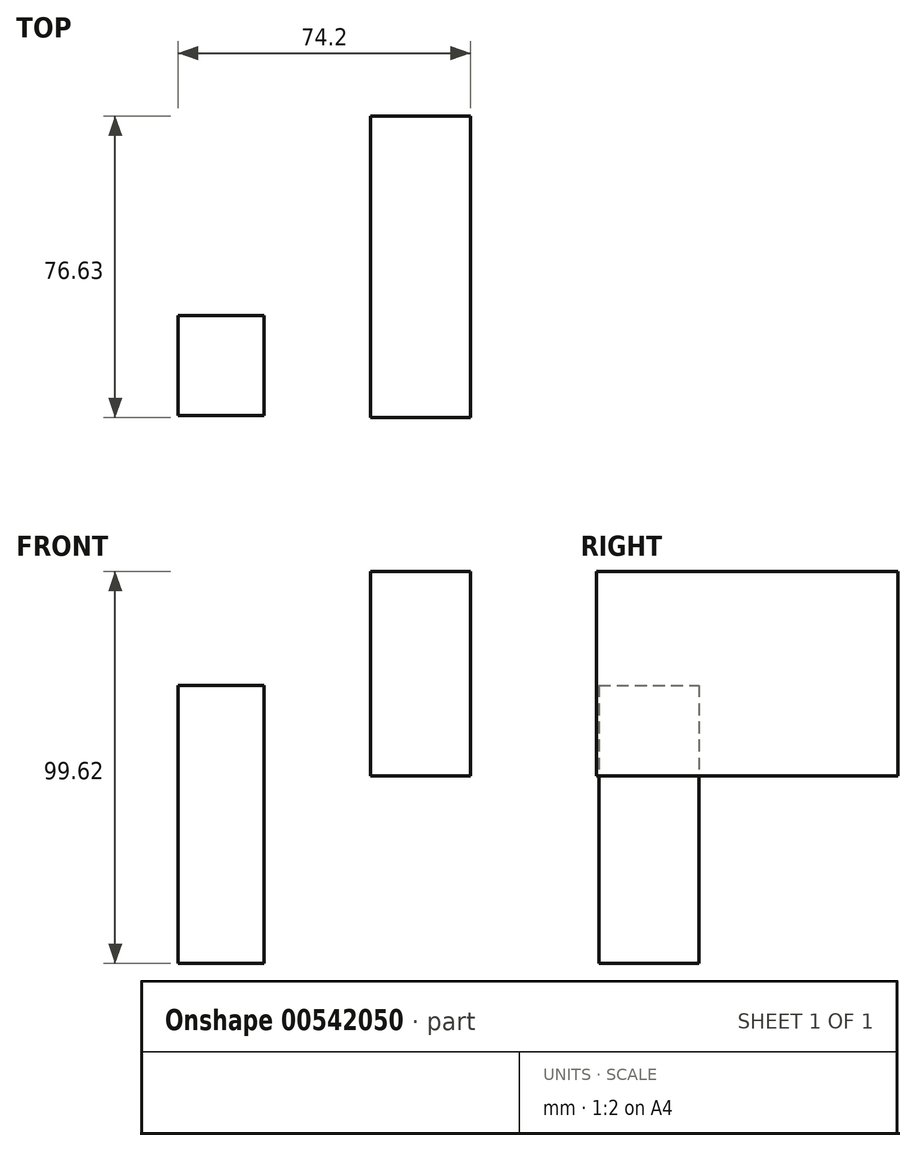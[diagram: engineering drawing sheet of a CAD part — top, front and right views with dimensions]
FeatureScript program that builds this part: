
annotation { "Feature Type Name" : "Feature", "Feature Type Description" : "" }
export const myFeature = defineFeature(function(context is Context, id is Id, definition is map)
    precondition{}
    {
        {
            var Q0;
            Q0=qCreatedBy(makeId("Front.planeOp"),FACE);
            var sketch = newSketch(context, id + "F0", { "sketchPlane" : qUnion([Q0])});
            skLineSegment(sketch, "E0.bottom", {"start": v(-48.8, 39.15) * mm, "end": v(-26.95, 39.15) * mm});
            skLineSegment(sketch, "E0.top", {"start": v(-48.8, -31.5) * mm, "end": v(-26.95, -31.5) * mm});
            skLineSegment(sketch, "E0.left", {"start": v(-48.8, 39.15) * mm, "end": v(-48.8, -31.5) * mm});
            skLineSegment(sketch, "E0.right", {"start": v(-26.95, 39.15) * mm, "end": v(-26.95, -31.5) * mm});
            skSolve(sketch);
        }
        {
            var Q0;
            Q0=makeQuery(id+"F0.imprint","IMPRINT",FACE,{"disambiguationData":[TD([[makeQuery(id+"F0.imprint","IMPRINT",EDGE,{"derivedFrom":sQuery(id+"F0.wireOp",EDGE,"E0.bottom")}),-1.0]])]});
            extrude(context, id + "F1", {"entities" : qUnion([Q0]), "depth" : 25.4 * mm, "offsetDistance" : 25.4 * mm});
        }
        {
            var Q0;
            Q0=qCreatedBy(makeId("Right.planeOp"), FACE);
            var sketch = newSketch(context, id + "F2", { "sketchPlane" : qUnion([Q0])});
            skLineSegment(sketch, "E1.bottom", {"start": v(-26.02, 68.13) * mm, "end": v(50.6, 68.13) * mm});
            skLineSegment(sketch, "E1.top", {"start": v(-26.02, 16.14) * mm, "end": v(50.6, 16.14) * mm});
            skLineSegment(sketch, "E1.left", {"start": v(-26.02, 68.13) * mm, "end": v(-26.02, 16.14) * mm});
            skLineSegment(sketch, "E1.right", {"start": v(50.6, 68.13) * mm, "end": v(50.6, 16.14) * mm});
            skLineSegment(sketch, "E2.bottom", {"start": v(41.07, 16.14) * mm, "end": v(0, 16.14) * mm});
            skLineSegment(sketch, "E2.top", {"start": v(41.07, 16.14) * mm, "end": v(0, 16.14) * mm});
            skLineSegment(sketch, "E2.left", {"start": v(41.07, 16.14) * mm, "end": v(41.07, 16.14) * mm});
            skLineSegment(sketch, "E2.right", {"start": v(0, 16.14) * mm, "end": v(0, 16.14) * mm});
            skSolve(sketch);
        }
        {
            var Q0;
            Q0 = qSketchRegion(id + "F2", true);
            extrude(context, id + "F3", {"entities" : qUnion([Q0]), "domain" : OperationDomain.MODEL, "flatOperationType" : FlatOperationType.REMOVE, "depth" : 25.4 * mm, "offsetDistance" : 25.4 * mm});
        }
    });
